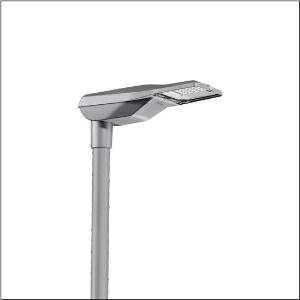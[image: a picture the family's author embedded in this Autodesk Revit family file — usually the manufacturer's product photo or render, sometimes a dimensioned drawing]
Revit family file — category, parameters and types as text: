
# Revit family: streetlight_sl_21_iq_micro___st0_8a_5xe1c21g08cb_23b1
name_source: partatom
category: Lighting Fixtures
units: mm (PartAtom-declared; Revit-internal decimal feet)

## family parameters
Cut with Voids When Loaded = No
Host = Face
Light Source = No
Part Type = Normal
Room Calculation Point = No
Round Connector Dimension = Use Diameter
Shared = No

## types (1)
- --- (1 x LED, 2380 lm, 19.4 W, 2200K)
    Apparent Load = 19 VA
    CIE Flux Codes = 38 75 97 100 100
    Color Rendering = 70
    Color Temperature = 2200K
    Default Elevation = 1800 mm
    Description = Streetlight SL 21 iQ micro, mast luminaire, primary light control with lens, of PMMA, primary optical cover: cover, of toughened safety glass, transparent, light distribution: ST0.8a, light emission: direct distribution, primary light characteristic: asymmetric, installation type: post-top, side-entry, LED, High Power LED, rated luminous flux: 2.380lm, luminous efficacy: 123lm/W, light colour: 722, colour temperature: 2200K, control gear: iQ Street-Remote, control: Street-Remote, Auto-Match, Temp-Guard, Lumen-Switch, Night-Set, Smart-Wire, Light-Fading, Desk-Remote (wireless, voltage-free reading and setting of iQ features in the workshop via application-optimized NFC function/RFID function), optimised constant luminous flux control (CLO 2.0), pre-setting: linear dimming characteristic, mains connection: 220..240V, AC, 50/60Hz, start of lifetime: 19W, end of service life: 20W, reduction: 10W, luminaire housing, of diecast aluminium, powder-coated, Siteco® metallic grey (DB 702S), corrosivity category C5 high according to DIN EN ISO 12944, please order mast flange separately, inclination adjustable: 0°, 5°, 10°, 15°, sealing non-destructively replaceable, multi-level sealing system, length: 528mm, width: 235mm, height: 110mm, mast flange for spigot size: 42mm (side-entry): 5XC10008XM4, 60/48mm (side-entry/post-top): 5XC10108XM2, 76/60mm (side-entry/post-top): 5XC10108XM1, protection rating (complete): IP66, insulation class (complete): insulation class II (safety insulation), certification: CE, ENEC, ENEC+, VDE, impact resistance: IK10, permissible operating ambient temperature for outdoor applications: -40..+50°C, standard-compliant lighting for roads and squares, packaging unit: 1 piece

Light Distribution: ST0.8a
    Height = 110 mm
    Lamp = 1 x LED
    Lamp Light Flux = 2380 lm
    Lamp Power = 19.4 W
    Lamp count = 1
    Length = 528 mm
    Luminous efficacy = 123 lm/W
    Manufacturer = Siteco
    ModVariant = No
    Model = 5XE1C21G08CB
    Number of Poles = 1
    OnlyDefault = Yes
    Power Factor = 1
    Product Name = Streetlight SL 21 iQ micro | ST0.8a
    Product group = mast luminaire | pylon top
    ProductGroupID = 6100
    Protection Class = Protection class II
    Protection Degree = IP 66
    RLX_Detail_Level = 1
    RLX_Emergency_Light_Flux = 0 lm
    RLX_Emergency_Type = 0
    RLX_Emergency_Type_DB = No
    RlxData = <blob elided: 99869 chars, md5=860dbd57>
    Socket = socket
    Standby Power = 0 W
    System Light Flux = 2380 lm
    System Power = 19 W
    Type Comments = factory setting: luminous flux: 100 % | dim-lin: 254 | 387 mA
    Type Image = l_1006881.jpg
    URL = http://relux.com
    VarID = @adj_141777
    Voltage = 0 V
    Weight = 0.00 kg
    Width = 235 mm

## geometry (parser evidence)
native form markers: Blend x4, Sweep x9
no freeform markers — native parametric forms only
